# Revit family: Тактильная плитка ПВХ линейное расположение (самоклеящаяся)
name_source: partatom
category: Оборудование
revit_build: Autodesk Revit 2017 (Build: 20160225_1515(x64)
units: mm (PartAtom-declared; Revit-internal decimal feet)

## family parameters
Общий = Да
Основа = Грань
При загрузке вырезать с полостями = Да
Размер круглого соединителя = Использовать диаметр
Тип детали = Нормальный
Точка расчета площади = Нет

## types (2) — shared parameters
ADSK_Наименование = Тактильная плитка ПВХ линейное расположение (самоклеящаяся)
ADSK_Размер_Высота рифа = 5 мм
ADSK_Размер_Габариты = 300Х300
ADSK_Размер_Длина = 300 мм
ADSK_Размер_Толщина = 2 мм
ADSK_Размер_Ширина = 300 мм
ADSK_Тип рифов = Конусообразные рифы, линейное расположение
URL = http://tiflocentre.ru
Изготовитель = ТИФЛОЦЕНТР «ВЕРТИКАЛЬ»
Применение = Улица/Помещение
Стоимость = 539 $
zero-valued in all types: Отметка по умолчанию

## per-type parameters (varying)
| type | ADSK_Код изделия | ADSK_Материал наименование | ADSK_Материал плитки | Описание |
| Тактильная плитка полиуретан дагональ_Желтая | 10653-1-ZH | Полиуретан, цвет желтый | Вертикаль_Полиуретан_Желтый | Тактильная самоклеящаяся плитка ПВХ необходима для передачи информировании при движении как для тотально слепого человека, так и для слабовидящего человека в зданиях. В зависимости от взаимного расположения с другими тактильными указателями несет различную тактильную информацию. В данной модели тактильные рифы расположены параллельно. Плитка с таким расположением рифов используется для информирования тотально незрячих людей о преодолимых препятствиях на пути.  Способ крепления - самоклеящаяся. Самоклеящаяся ПВХ плитка рекомендована к применению ВОС и протестирована незрячими специалистами. |
| Тактильная плитка полиуретановая_Черная | 10653-1-CH | Полиуретан, цвет черный | Вертикаль_Полиуретан_Черный | Тактильная ПВХ плитка предназначена для информирования при движении тотально слепого и слабовидящего человека. Черный цвет тактильной плитки - отличный контраст по отношению к светлым стенам и покрытию. В зависимости от взаимного расположения несет различную тактильную информацию, способ крепления самоклеящаяся. Рекомендован к применению ВОС, гос. программой "Доступная среда". |
